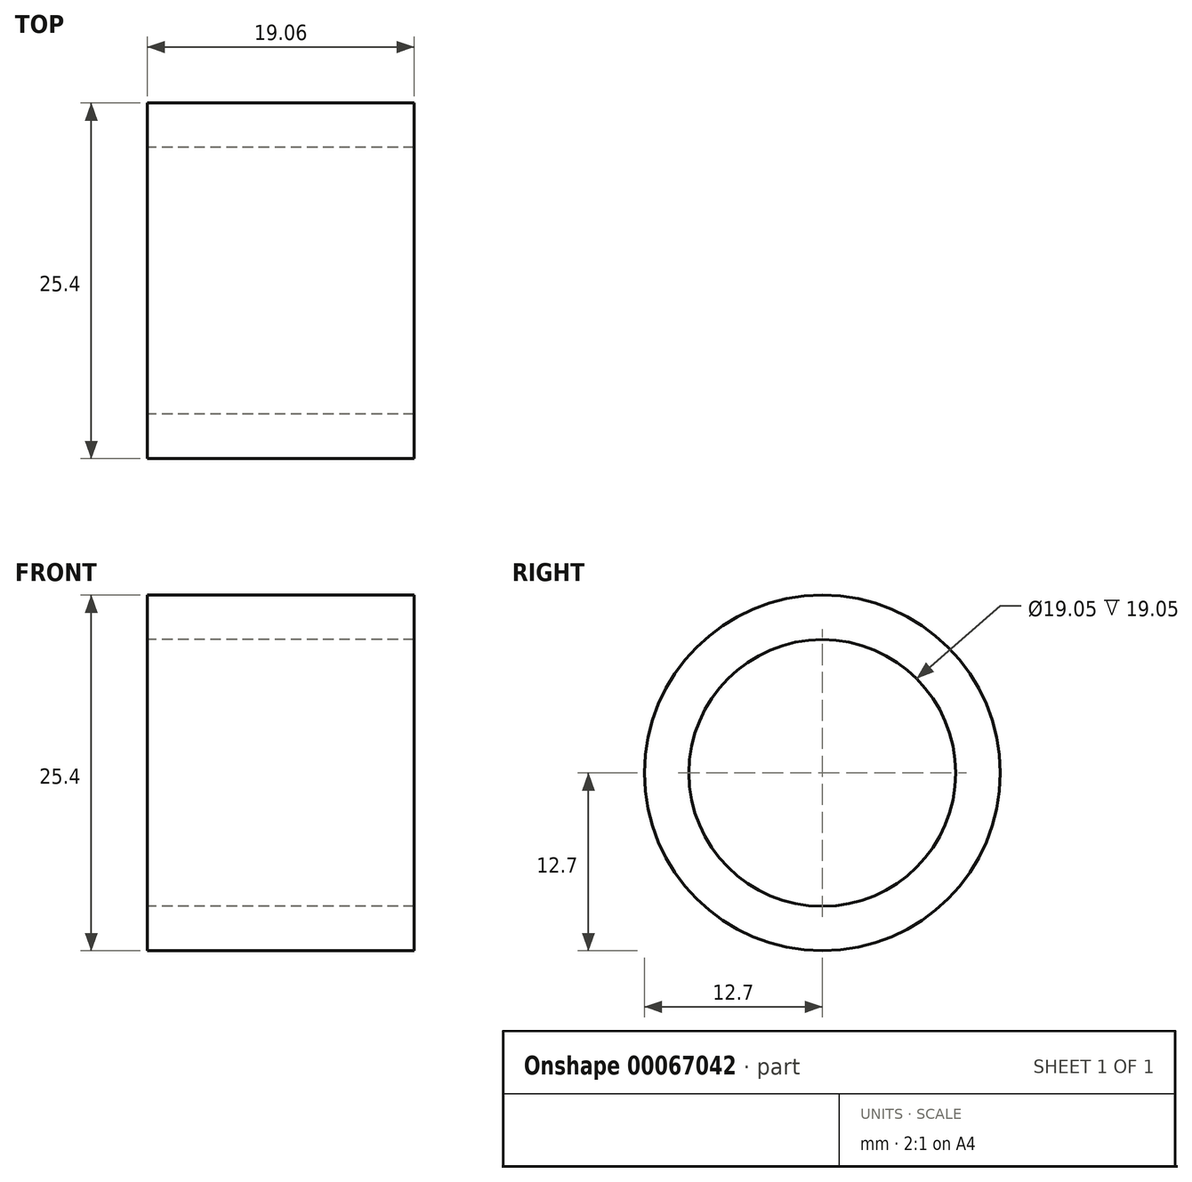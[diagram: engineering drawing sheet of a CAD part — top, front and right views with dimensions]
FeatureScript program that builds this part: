
annotation { "Feature Type Name" : "Feature", "Feature Type Description" : "" }
export const myFeature = defineFeature(function(context is Context, id is Id, definition is map)
    precondition{}
    {
        {
            var Q0;
            Q0=qCreatedBy(makeId("Right.planeOp"),FACE);
            var sketch = newSketch(context, id + "F0", { "sketchPlane" : qUnion([Q0])});
            skCircle(sketch, "E0", {"center": v(0, 0) * mm, "radius": 9.53 * mm});
            skCircle(sketch, "E1", {"center": v(0, 0) * mm, "radius": 12.7 * mm});
            skSolve(sketch);
        }
        {
            var Q0;
            Q0=qSketchRegion(id+"F0",true);
            extrude(context, id + "F1", {"entities" : qUnion([Q0]), "endBound" : BoundingType.SYMMETRIC, "depth" : 19.05 * mm});
        }
    });
